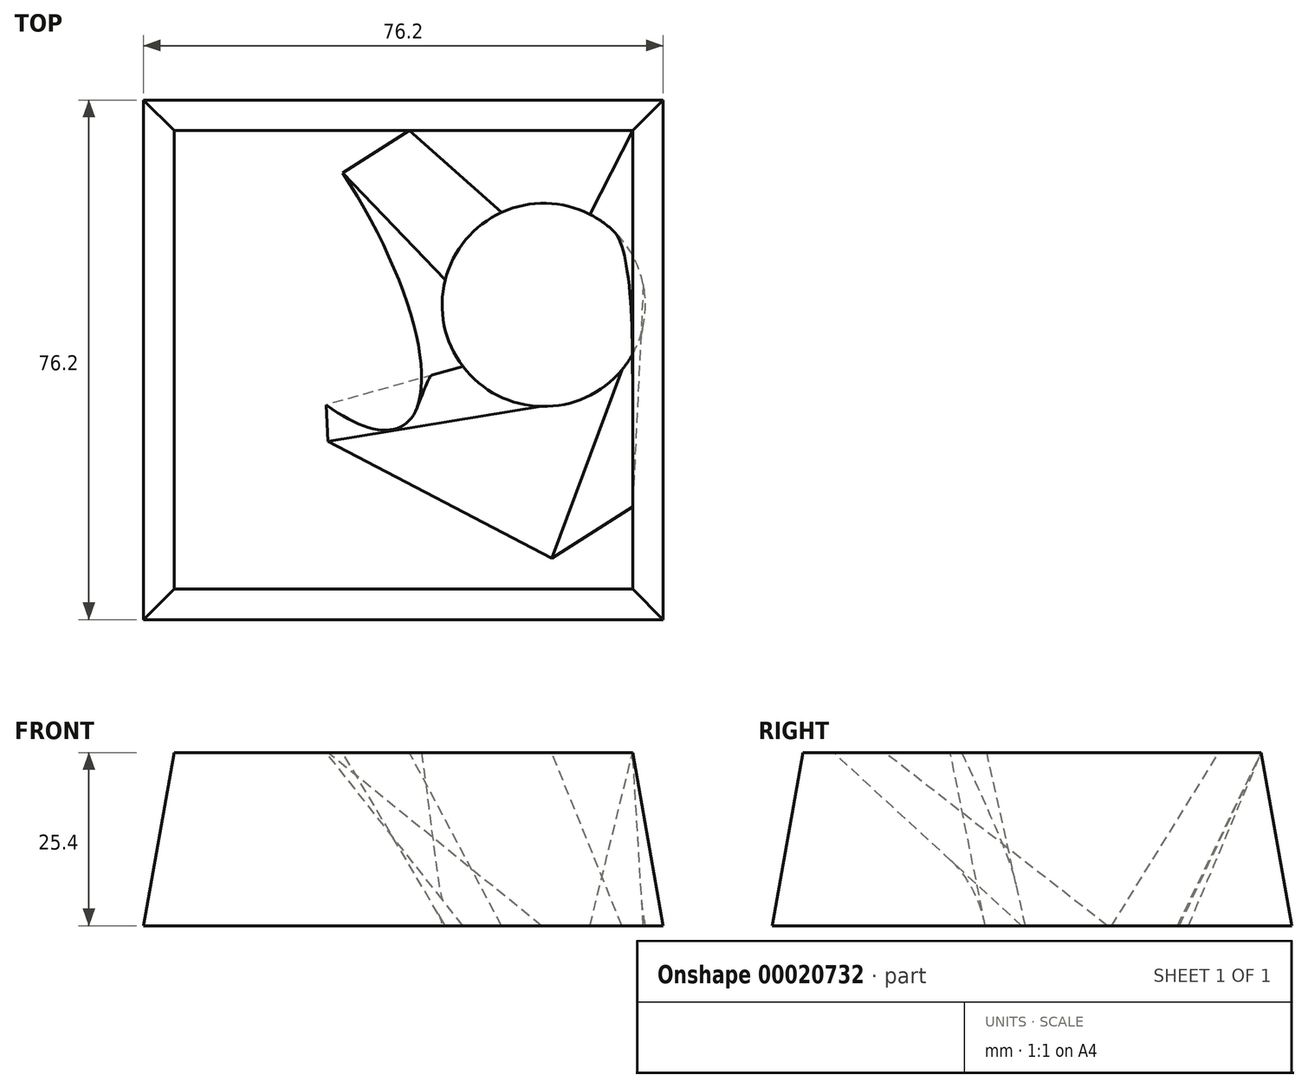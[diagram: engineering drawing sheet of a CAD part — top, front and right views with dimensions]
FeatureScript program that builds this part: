
annotation { "Feature Type Name" : "Feature", "Feature Type Description" : "" }
export const myFeature = defineFeature(function(context is Context, id is Id, definition is map)
    precondition{}
    {
        {
            var Q0;
            Q0=qCreatedBy(makeId("Top.planeOp"),FACE);
            var sketch = newSketch(context, id + "F0", { "sketchPlane" : qUnion([Q0])});
            skLineSegment(sketch, "E0.bottom", {"start": v(0, 0) * mm, "end": v(76.2, 0) * mm});
            skLineSegment(sketch, "E0.top", {"start": v(0, 76.2) * mm, "end": v(76.2, 76.2) * mm});
            skLineSegment(sketch, "E0.left", {"start": v(0, 0) * mm, "end": v(0, 76.2) * mm});
            skLineSegment(sketch, "E0.right", {"start": v(76.2, 0) * mm, "end": v(76.2, 76.2) * mm});
            skSolve(sketch);
        }
        {
            var Q0;
            Q0 = qSketchRegion(id + "F0", true);
            extrude(context, id + "F1", {"entities" : qUnion([Q0]), "depth" : 25.4 * mm, "hasDraft" : true, "draftAngle" : 10 * degree, "draftPullDirection" : true});
        }
        {
            var Q0;
            Q0=makeQuery(id+"F1.opExtrude","CAP_FACE",FACE,{"disambiguationData":[OSD([sQuery(id+"F0.wireOp",EDGE,"E0.bottom"),sQuery(id+"F0.wireOp",EDGE,"E0.top"),sQuery(id+"F0.wireOp",EDGE,"E0.left"),sQuery(id+"F0.wireOp",EDGE,"E0.right")])],"isStart":false});
            var sketch = newSketch(context, id + "F2", { "sketchPlane" : qUnion([Q0])});
            skEllipse(sketch, "E1", {"center": v(19.96, 57.53) * mm, "majorRadius": 34.25 * mm, "minorRadius": 12.1 * mm, "majorAxis": v(0.53, -0.85)});
            skSolve(sketch);
        }
        {
            var Q0;
            {var subQ3=makeQuery(id+"F1.opExtrude","CAP_EDGE",EDGE,{"disambiguationData":[OSD([sQuery(id+"F0.wireOp",EDGE,"E0.bottom")])],"isStart":false});Q0=makeQuery(id+"F2.imprint","IMPRINT",FACE,{"disambiguationData":[TD([[makeQuery(id+"F2.imprint","IMPRINT",EDGE,{"derivedFrom":subQ3}),1.0]])]});}
            var sketch = newSketch(context, id + "F3", { "sketchPlane" : qUnion([Q0])});
            skCircle(sketch, "E2.cCircle", {"center": v(58.28, 46) * mm, "radius": 32.07 * mm, "construction": true});
            skLineSegment(sketch, "E2.0", {"start": v(59.86, 9) * mm, "end": v(27.03, 26.12) * mm});
            skLineSegment(sketch, "E2.1", {"start": v(27.03, 26.12) * mm, "end": v(25.45, 63.13) * mm});
            skLineSegment(sketch, "E2.2", {"start": v(25.45, 63.13) * mm, "end": v(56.7, 83) * mm});
            skLineSegment(sketch, "E2.3", {"start": v(56.7, 83) * mm, "end": v(89.54, 65.86) * mm});
            skLineSegment(sketch, "E2.4", {"start": v(89.54, 65.86) * mm, "end": v(91.12, 28.86) * mm});
            skLineSegment(sketch, "E2.5", {"start": v(91.12, 28.86) * mm, "end": v(59.86, 9) * mm});
            skPoint(sketch, "E2.0.midPoint", {"position": v(43.45, 17.56) * mm});
            skSolve(sketch);
        }
        {
            var Q0;
            {var subQ3=makeQuery(id+"F1.opExtrude","CAP_EDGE",EDGE,{"disambiguationData":[OSD([sQuery(id+"F0.wireOp",EDGE,"E0.bottom")])],"isStart":false});Q0=makeQuery(id+"F2.imprint","IMPRINT",FACE,{"disambiguationData":[TD([[makeQuery(id+"F2.imprint","IMPRINT",EDGE,{"derivedFrom":subQ3}),1.0]])]});}
            cPlane(context, id + "F4", {"entities" : qUnion([Q0]), "cplaneType" : CPlaneType.OFFSET, "offset" : 6.35 * mm, "oppositeDirection" : true, "width" : 152.4 * mm, "height" : 152.4 * mm});
        }
        {
            var Q0;
            Q0=makeQuery(id+"F0.imprint","IMPRINT",FACE,{"disambiguationData":[TD([[makeQuery(id+"F0.imprint","IMPRINT",EDGE,{"derivedFrom":sQuery(id+"F0.wireOp",EDGE,"E0.bottom")}),1.0]])]});
            var sketch = newSketch(context, id + "F5", { "sketchPlane" : qUnion([Q0])});
            skCircle(sketch, "E3", {"center": v(58.7, 46.15) * mm, "radius": 14.9 * mm});
            skSolve(sketch);
        }
        {
            var Q1;
            Q1=makeQuery(id+"F5.imprint","IMPRINT",FACE,{"disambiguationData":[TD([[makeQuery(id+"F5.imprint","IMPRINT",EDGE,{"derivedFrom":sQuery(id+"F5.wireOp",EDGE,"E3")}),1.0]])]});
            var Q2;
            Q2=makeQuery(id+"F3.imprint","IMPRINT",FACE,{"disambiguationData":[TD([[makeQuery(id+"F3.imprint","IMPRINT",EDGE,{"derivedFrom":sQuery(id+"F3.wireOp",EDGE,"E2.0")}),-1.0]])]});
            loft(context, id + "F6", {"operationType" : NewBodyOperationType.REMOVE, "sheetProfilesArray" : [{ "sheetProfileEntities" : qUnion([Q1]) }, { "sheetProfileEntities" : qUnion([Q2]) }]});
        }
    });
